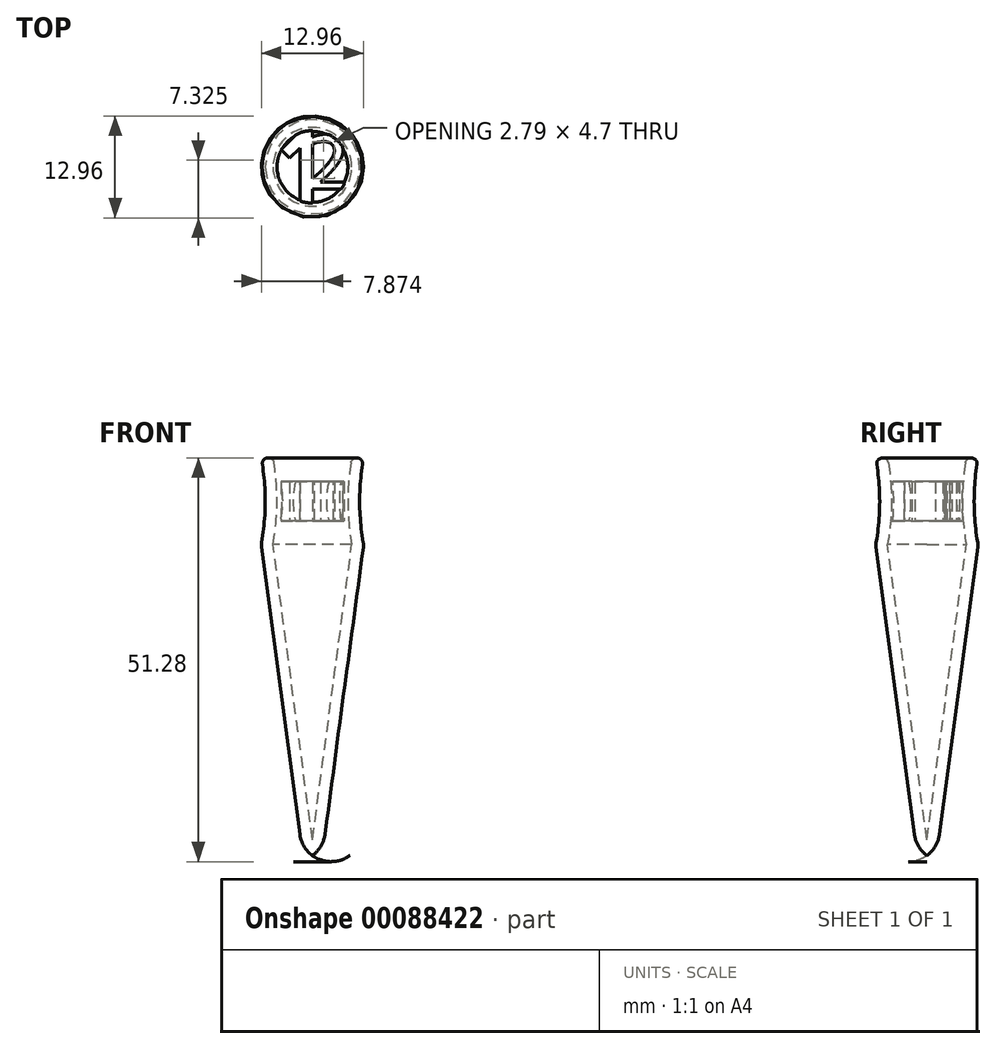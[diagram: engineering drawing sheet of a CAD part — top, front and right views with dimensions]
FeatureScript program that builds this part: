
annotation { "Feature Type Name" : "Feature", "Feature Type Description" : "" }
export const myFeature = defineFeature(function(context is Context, id is Id, definition is map)
    precondition{}
    {
        {
            var Q0;
            Q0=qCreatedBy(makeId("Right.planeOp"),FACE);
            var sketch = newSketch(context, id + "F0", { "sketchPlane" : qUnion([Q0])});
            skLineSegment(sketch, "E0", {"start": v(0, 0) * mm, "end": v(0, 5.87) * mm, "construction": true});
            skLineSegment(sketch, "E1", {"start": v(4.5, 0) * mm, "end": v(6, 0) * mm});
            skLineSegment(sketch, "E2", {"start": v(5, 5.5) * mm, "end": v(6.5, 5.5) * mm});
            skLineSegment(sketch, "E3", {"start": v(6, 0) * mm, "end": v(6, -1.82) * mm, "construction": true});
            skArc(sketch, "E4", {"start": v(6, 0) * mm, "mid": v(6.13, 2.76) * mm, "end": v(6.5, 5.5) * mm});
            skLineSegment(sketch, "E5", {"start": v(4.5, 0) * mm, "end": v(4.5, -1.86) * mm, "construction": true});
            skArc(sketch, "E6", {"start": v(4.5, 0) * mm, "mid": v(4.63, 2.76) * mm, "end": v(5, 5.5) * mm});
            skSolve(sketch);
        }
        {
            var Q0;
            Q0=makeQuery(id+"F0.imprint","IMPRINT",FACE,{"disambiguationData":[TD([[makeQuery(id+"F0.imprint","IMPRINT",EDGE,{"derivedFrom":sQuery(id+"F0.wireOp",EDGE,"E1")}),1.0]])]});
            var Q1;
            Q1=sQuery(id+"F0.wireOp",EDGE,"E0");
            revolve(context, id + "F1", {"entities" : qUnion([Q0]), "axis" : qUnion([Q1]), "revolveType" : RevolveType.FULL});
        }
        {
            var Q0;
            Q0=makeQuery(id+"F1.opRevolve","SWEPT_BODY",BODY,{"disambiguationData":[OSD([sQuery(id+"F0.wireOp",EDGE,"E1"),sQuery(id+"F0.wireOp",EDGE,"E2"),sQuery(id+"F0.wireOp",EDGE,"E4"),sQuery(id+"F0.wireOp",EDGE,"E6")])]});
            var Q1;
            Q1=qCreatedBy(makeId("Top.planeOp"),FACE);
            mirror(context, id + "F2", {"operationType" : NewBodyOperationType.ADD, "entities" : qUnion([Q0]), "mirrorPlane" : qUnion([Q1])});
        }
        {
            var Q0;
            Q0=makeQuery(id+"F1.opRevolve","SWEPT_FACE",FACE,{"disambiguationData":[OSD([sQuery(id+"F0.wireOp",EDGE,"E2")])]});
            fillet(context, id + "F3", {"entities" : qUnion([Q0]), "radius" : .7 * mm, "tangentPropagation" : true, "allowEdgeOverflow" : false});
        }
        {
            var Q0;
            Q0=qCreatedBy(makeId("Top.planeOp"),FACE);
            var sketch = newSketch(context, id + "F4", { "sketchPlane" : qUnion([Q0])});
            skText(sketch, "E7", { "text": "1", "fontName": "AllertaStencil-Regular.ttf"});
            skText(sketch, "E8", { "text": "2", "fontName": "AllertaStencil-Regular.ttf"});
            const initialGuessF4  = {"E7": [-0.00438, -0.0049, 1, 0, 0.00955], "E8": [-0.00113, -0.00283, 1, 0, 0.00693]};
            skSetInitialGuess(sketch, initialGuessF4);
            skSolve(sketch);
        }
        {
            var Q0;
            Q0=qSketchRegion(id+"F4",true);
            extrude(context, id + "F5", {"entities" : qUnion([Q0]), "operationType" : NewBodyOperationType.ADD, "endBound" : BoundingType.SYMMETRIC, "depth" : 5 * mm});
        }
        {
            var Q0;
            Q0=qCreatedBy(makeId("Top.planeOp"),FACE);
            var sketch = newSketch(context, id + "F6", { "sketchPlane" : qUnion([Q0])});
            skText(sketch, "E9", { "text": "1", "fontName": "AllertaStencil-Regular.ttf"});
            skText(sketch, "E10", { "text": "3", "fontName": "AllertaStencil-Regular.ttf"});
            const initialGuessF6  = {"E9": [-0.00439, -0.0049, 1, 0, 0.00953], "E10": [-0.00095, -0.00271, 1, 0, 0.00693]};
            skSetInitialGuess(sketch, initialGuessF6);
            skSolve(sketch);
        }
        {
            var Q0;
            Q0=qCreatedBy(makeId("Front.planeOp"),FACE);
            var sketch = newSketch(context, id + "F7", { "sketchPlane" : qUnion([Q0])});
            skLineSegment(sketch, "E11", {"start": v(5, -5.5) * mm, "end": v(6.5, -5.5) * mm});
            skLineSegment(sketch, "E12", {"start": v(0, 13.26) * mm, "end": v(0, 0) * mm, "construction": true});
            skLineSegment(sketch, "E13", {"start": v(6.5, -5.5) * mm, "end": v(1.6, -42.3) * mm});
            skLineSegment(sketch, "E14", {"start": v(5, -5.5) * mm, "end": v(0, -43) * mm});
            skLineSegment(sketch, "E15", {"start": v(0, -43) * mm, "end": v(0, -45) * mm});
            skArc(sketch, "E16", {"start": v(1.6, -42.3) * mm, "mid": v(1.07, -43.82) * mm, "end": v(0, -45) * mm});
            skSolve(sketch);
        }
        {
            var Q0;
            Q0=makeQuery(id+"F7.imprint","IMPRINT",FACE,{"disambiguationData":[TD([[makeQuery(id+"F7.imprint","IMPRINT",EDGE,{"derivedFrom":sQuery(id+"F7.wireOp",EDGE,"E11")}),-1.0]])]});
            var Q1;
            Q1=sQuery(id+"F7.wireOp",EDGE,"E12");
            revolve(context, id + "F8", {"operationType" : NewBodyOperationType.ADD, "entities" : qUnion([Q0]), "axis" : qUnion([Q1]), "revolveType" : RevolveType.ONE_DIRECTION, "angle" : 360 * degree});
        }
        {
            var Q0;
            Q0=makeQuery(id+"F8.boolean.opBoolean","MERGE",EDGE,{"derivedFrom":[makeQuery(id+"F2.opPattern","COPY",EDGE,{"derivedFrom":makeQuery(id+"F1.opRevolve","SWEPT_EDGE",EDGE,{"disambiguationData":[OSD([sQuery(id+"F0.wireOp",EDGE,"E2"),sQuery(id+"F0.wireOp",EDGE,"E4")])]}),"instanceName":"1"}),makeQuery(id+"F8.opRevolve","SWEPT_EDGE",EDGE,{"disambiguationData":[OSD([sQuery(id+"F7.wireOp",EDGE,"E11"),sQuery(id+"F7.wireOp",EDGE,"E13")])]})]});
            fillet(context, id + "F9", {"entities" : qUnion([Q0]), "radius" : 2 * mm, "tangentPropagation" : true, "allowEdgeOverflow" : false});
        }
    });
